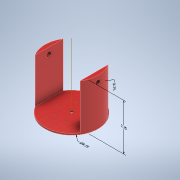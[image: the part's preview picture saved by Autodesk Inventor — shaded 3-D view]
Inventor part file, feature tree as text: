
AUTODESK INVENTOR PART (.ipt)
format: ipt  version: 2021 (Build 250183000, 183)  size: 160,768 bytes
history: native  units: in
note: dims shown in document units (in); Inventor stores cm internally (conversion verified against a paired STEP export)
features: sketch x5, other x4, extrude x4, mirror x1, plane x1, hole x1, pattern_circular x1
ambient origin geometry x8: Origin, YZ Plane, XZ Plane, XY Plane, X Axis, Y Axis, Z Axis, Center Point
bodies: Solid1 (feature_tree)
feature tree (17):
  other  "Annotations"
  extrude  "Extrusion1"  TaperAngle=0.0deg  [1 undecoded]
  extrude  "Extrusion7"  TaperAngle=0.0deg  [1 undecoded]
  mirror  "Mirror1"
  plane  "Work Plane2"
  extrude  "Extrusion8"  TaperAngle=0.0deg  [1 undecoded]
  extrude  "Extrusion9"  Depth=7.25in TaperAngle=360.0deg
  hole  "Hole1"  [1 undecoded]
  pattern_circular  "Circular Pattern2"  [2 undecoded]
  sketch  "Sketch1"  dims[d3=0.0in d33=0.0in]
  sketch  "Sketch7"  dims[d34=0.75in d35=0.0in d36=0.0in]
  sketch  "Sketch8"  dims[d47=0.5in d48=0.0in d49=0.0in]
  sketch  "Sketch9"  dims[d50=2.0in]
  sketch  "Sketch10"  dims[d51=0.266in d52=0.75in d53=0.438in d54=0.25in d55=0.5635in d56=1.0in d57=0.8108in d58=2.3622in d59=360.0deg d38=0.263in d39=0.2869in d40=7.25in d41=1.9973in d42=0.1836in d43=0.3337in d44=0.75in d45=0.2596in d46=8.25in]
  other  "Linear Dimension 1"
  other  "Diameter Dimension 1"
  other  "Diameter Dimension 2"
note: 6 required parameter values undecoded (feature->parameter linkage not recoverable at this tier; creation-order binding heuristic only, values carry confidence <= 0.55)
